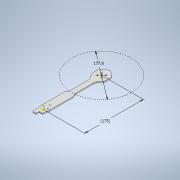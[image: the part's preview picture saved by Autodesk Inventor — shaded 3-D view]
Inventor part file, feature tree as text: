
AUTODESK INVENTOR PART (.ipt)
format: ipt  version: 2020 (Build 240168000, 168)  size: 245,248 bytes
history: native  units: in
note: dims shown in document units (in); Inventor stores cm internally (conversion verified against a paired STEP export)
features: sketch x3, extrude x2, fillet x1
ambient origin geometry x8: Origin, YZ Plane, XZ Plane, XY Plane, X Axis, Y Axis, Z Axis, Center Point
bodies: Body1 (feature_tree)
feature tree (6):
  extrude  "Extrusion1"  Depth=0.1181in
  sketch  "Sketch4"  dims[d7=0.4724in d9=7.0in d10=6.8898in]
  extrude  "Extrusion2"  Depth=7.0in
  fillet  "Fillet1"  Radius=6.8898in
  sketch  "Sketch3"  dims[d2=0.1181in d3=0.0in d4=0.8352in]
  sketch  "Sketch5"  dims[d11=6.8898in d12=0.2953in d13=0.2953in d14=0.9835in d15=0.9835in d16=0.9835in d17=0.1181in d18=0.0in d19=0.3937in]
